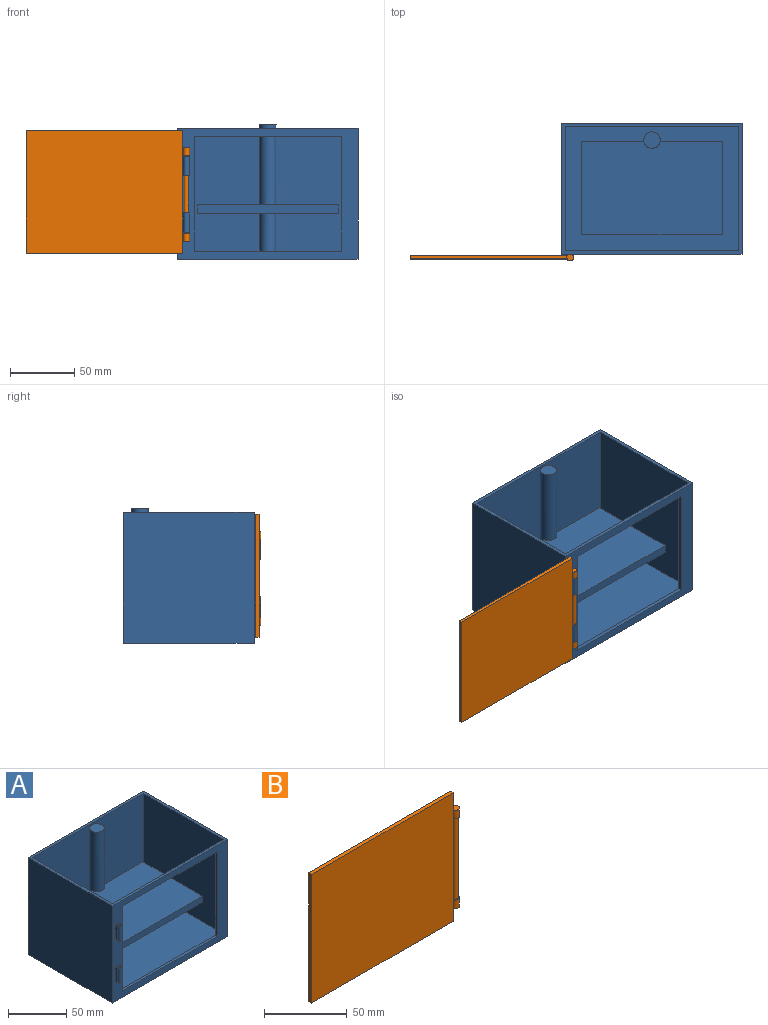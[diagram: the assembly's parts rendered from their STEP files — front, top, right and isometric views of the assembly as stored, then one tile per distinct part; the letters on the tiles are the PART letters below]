
ASSEMBLY  parts=2 mates=1
PART A: 36 faces, bbox 139.7x106.7x104.4 mm
  f0: plane 139.7x101.6mm, normal (0,-1,0), area 3877.4mm2, adj f2,f3,f4,f5,f11,f12,f13,f14
  f1: plane 134.62x99.06mm, normal (0,1,0), area 3174.2mm2, adj f2,f7,f8,f9,f11,f12,f13,f14
  f2: plane 139.7x101.6mm, normal (0,0,1), area 1200mm2, adj f0,f1,f3,f5,f6,f7,f9,f10
  f3: plane 101.6x101.6mm, normal (-1,0,0), area 10322.6mm2, adj f0,f2,f4,f6
  f4: plane 139.7x101.6mm, normal (0,0,-1), area 14193.5mm2, adj f0,f3,f5,f6
  f5: plane 101.6x101.6mm, normal (1,0,0), area 10322.6mm2, adj f0,f2,f4,f6
  f6: plane 139.7x101.6mm, normal (0,1,0), area 14193.5mm2, adj f2,f3,f4,f5
  f7: plane 99.06x96.52mm, normal (1,0,0), area 9561.3mm2, adj f1,f2,f8,f10
  f8: plane 134.62x96.52mm, normal (0,0,1), area 12866.8mm2, adj f1,f7,f9,f10,f27
  f9: plane 99.06x96.52mm, normal (-1,0,0), area 9561.3mm2, adj f1,f2,f8,f10
  f10: plane 134.62x99.06mm, normal (0,-1,0), area 13335.5mm2, adj f2,f7,f8,f9
  f11: plane 114.3x2.54mm, normal (0,0,-1), area 290.3mm2, adj f0,f1,f12,f14
  f12: plane 88.9x2.54mm, normal (1,0,0), area 225.8mm2, adj f0,f1,f11,f13
  f13: plane 114.3x2.54mm, normal (0,0,1), area 290.3mm2, adj f0,f1,f12,f14
  f14: plane 88.9x2.54mm, normal (-1,0,0), area 225.8mm2, adj f0,f1,f11,f13
  f15: plane 5.08x5.08mm, normal (0,0,1), area 11.6mm2, adj f0,f16,f18,f23,f26
  f16: plane 15.24x2.54mm, normal (-1,0,0), area 38.7mm2, adj f0,f15,f17,f23
  f17: plane 5.08x5.08mm, normal (0,0,-1), area 11.6mm2, adj f0,f16,f18,f23,f26
  f18: plane 15.24x2.54mm, normal (1,0,0), area 38.7mm2, adj f0,f15,f17,f23
  f19: plane 5.08x5.08mm, normal (0,0,1), area 11.6mm2, adj f0,f20,f22,f24,f25
  f20: plane 15.24x2.54mm, normal (-1,0,0), area 38.7mm2, adj f0,f19,f21,f24
  f21: plane 5.08x5.08mm, normal (0,0,-1), area 11.6mm2, adj f0,f20,f22,f24,f25
  f22: plane 15.24x2.54mm, normal (1,0,0), area 38.7mm2, adj f0,f19,f21,f24
  f23: cylinder r=2.54mm len=15.24mm, axis (0,0,1), area 121.6mm2, adj f15,f16,f17,f18
  f24: cylinder r=2.54mm len=15.24mm, axis (0,0,1), area 121.6mm2, adj f19,f20,f21,f22
  f25: cylinder r=1.91mm len=15.24mm, axis (0,0,1), area 182.4mm2, adj f19,f21
  f26: cylinder r=1.91mm len=15.24mm, axis (0,0,1), area 182.4mm2, adj f15,f17
  f27: cylinder r=6.35mm len=101.85mm, axis (0,0,-1), area 3950.4mm2, adj f8,f28,f29,f30,f34,f35
  f28: plane 12.7x12.7mm, normal (0,0,1), area 126.7mm2, adj f27
  f29: plane 48.35x6.35mm, normal (0,1,0), area 307mm2, adj f27,f33,f34,f35
  f30: plane 48.35x6.35mm, normal (0,1,0), area 307mm2, adj f27,f31,f34,f35
  f31: plane 72.23x6.35mm, normal (-1,0,0), area 458.6mm2, adj f30,f32,f34,f35
  f32: plane 109.22x6.35mm, normal (0,-1,0), area 693.5mm2, adj f31,f33,f34,f35
  f33: plane 72.23x6.35mm, normal (1,0,0), area 458.6mm2, adj f29,f32,f34,f35
  f34: plane 109.22x72.23mm, normal (0,0,1), area 7838.5mm2, adj f27,f29,f30,f31,f32,f33
  f35: plane 109.22x72.23mm, normal (0,0,-1), area 7838.5mm2, adj f27,f29,f30,f31,f32,f33
PART B: 13 faces, bbox 126.9x5.3x95.3 mm
  f0: cylinder r=1.82mm len=60.2mm, axis (0,0,1), area 686.9mm2, adj f3,f6
  f1: cylinder r=2.67mm len=6.35mm, axis (0,0,-1), area 103.1mm2, adj f2,f3,f10
  f2: plane 5.33x5.32mm, normal (0,0,1), area 22.3mm2, adj f1,f10
  f3: plane 5.33x5.32mm, normal (0,0,-1), area 12mm2, adj f0,f1,f10
  f4: cylinder r=2.67mm len=6.35mm, axis (0,0,1), area 103.1mm2, adj f5,f6,f10
  f5: plane 5.33x5.32mm, normal (0,0,-1), area 22.3mm2, adj f4,f10
  f6: plane 5.33x5.32mm, normal (0,0,1), area 12mm2, adj f0,f4,f10
  f7: plane 121.54x2.54mm, normal (0,0,1), area 308.7mm2, adj f8,f10,f11,f12
  f8: plane 95.25x2.54mm, normal (-1,0,0), area 241.9mm2, adj f7,f9,f11,f12
  f9: plane 121.54x2.54mm, normal (0,0,-1), area 308.7mm2, adj f8,f10,f11,f12
  f10: plane 95.25x2.54mm, normal (1,0,0), area 235.3mm2, adj f1,f2,f3,f4,f5,f6,f7,f9
  f11: plane 121.54x95.25mm, normal (0,-1,0), area 11576.6mm2, adj f7,f8,f9,f10
  f12: plane 121.54x95.25mm, normal (0,1,0), area 11576.6mm2, adj f7,f8,f9,f10
PLACE A t=(139.79,-4.07,55.73)mm fixed
PLACE B rot(axis=(0,0,1),0deg) t=(76.29,-6.61,57.48)mm
MATE revolute B.f0 <-> A.f23  axis (0,0,-1) through (78.11,-6.61,92.86)mm
